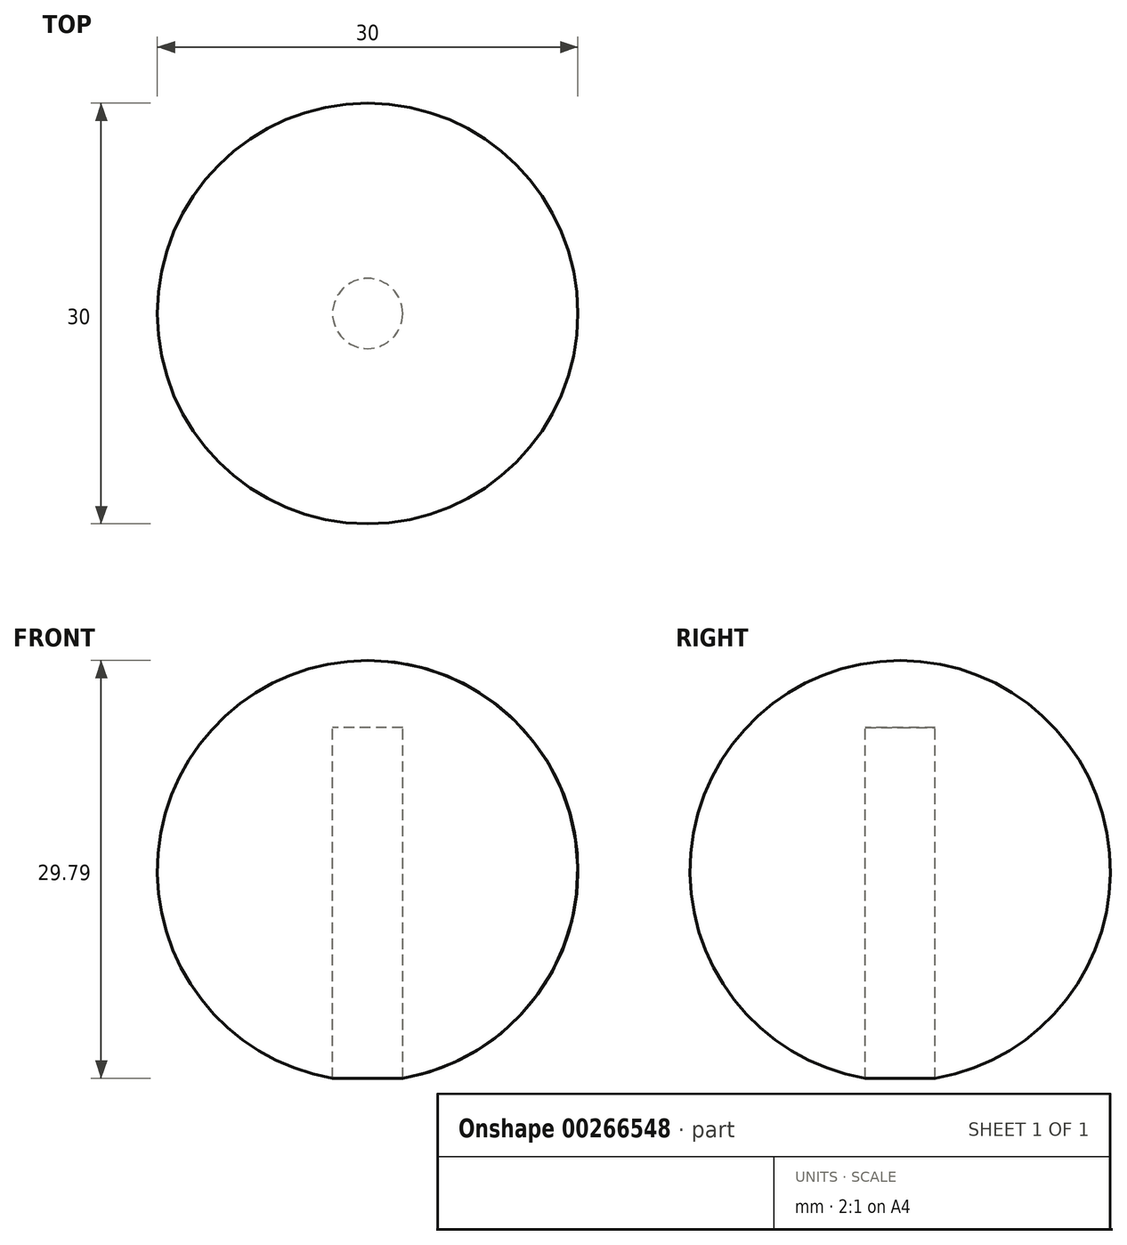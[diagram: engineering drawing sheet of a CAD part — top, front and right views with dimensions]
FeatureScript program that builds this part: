
annotation { "Feature Type Name" : "Feature", "Feature Type Description" : "" }
export const myFeature = defineFeature(function(context is Context, id is Id, definition is map)
    precondition{}
    {
        {
            var Q0;
            Q0=qCreatedBy(makeId("Front.planeOp"),FACE);
            var sketch = newSketch(context, id + "F0", { "sketchPlane" : qUnion([Q0])});
            skArc(sketch, "E0", {"start": v(2.5, 0.2) * mm, "mid": v(14.95, 16.25) * mm, "end": v(0, 30) * mm});
            skLineSegment(sketch, "E1", {"start": v(0, 30) * mm, "end": v(0, 25.2) * mm});
            skLineSegment(sketch, "E2", {"start": v(0, 25.2) * mm, "end": v(2.5, 25.2) * mm});
            skLineSegment(sketch, "E3", {"start": v(2.5, 25.2) * mm, "end": v(2.5, 0.2) * mm});
            skSolve(sketch);
        }
        {
            var Q0;
            Q0 = qSketchRegion(id + "F0", true);
            var Q1;
            Q1=sQuery(id+"F0.wireOp",EDGE,"E1");
            revolve(context, id + "F1", {"entities" : qUnion([Q0]), "axis" : qUnion([Q1]), "revolveType" : RevolveType.FULL});
        }
    });
